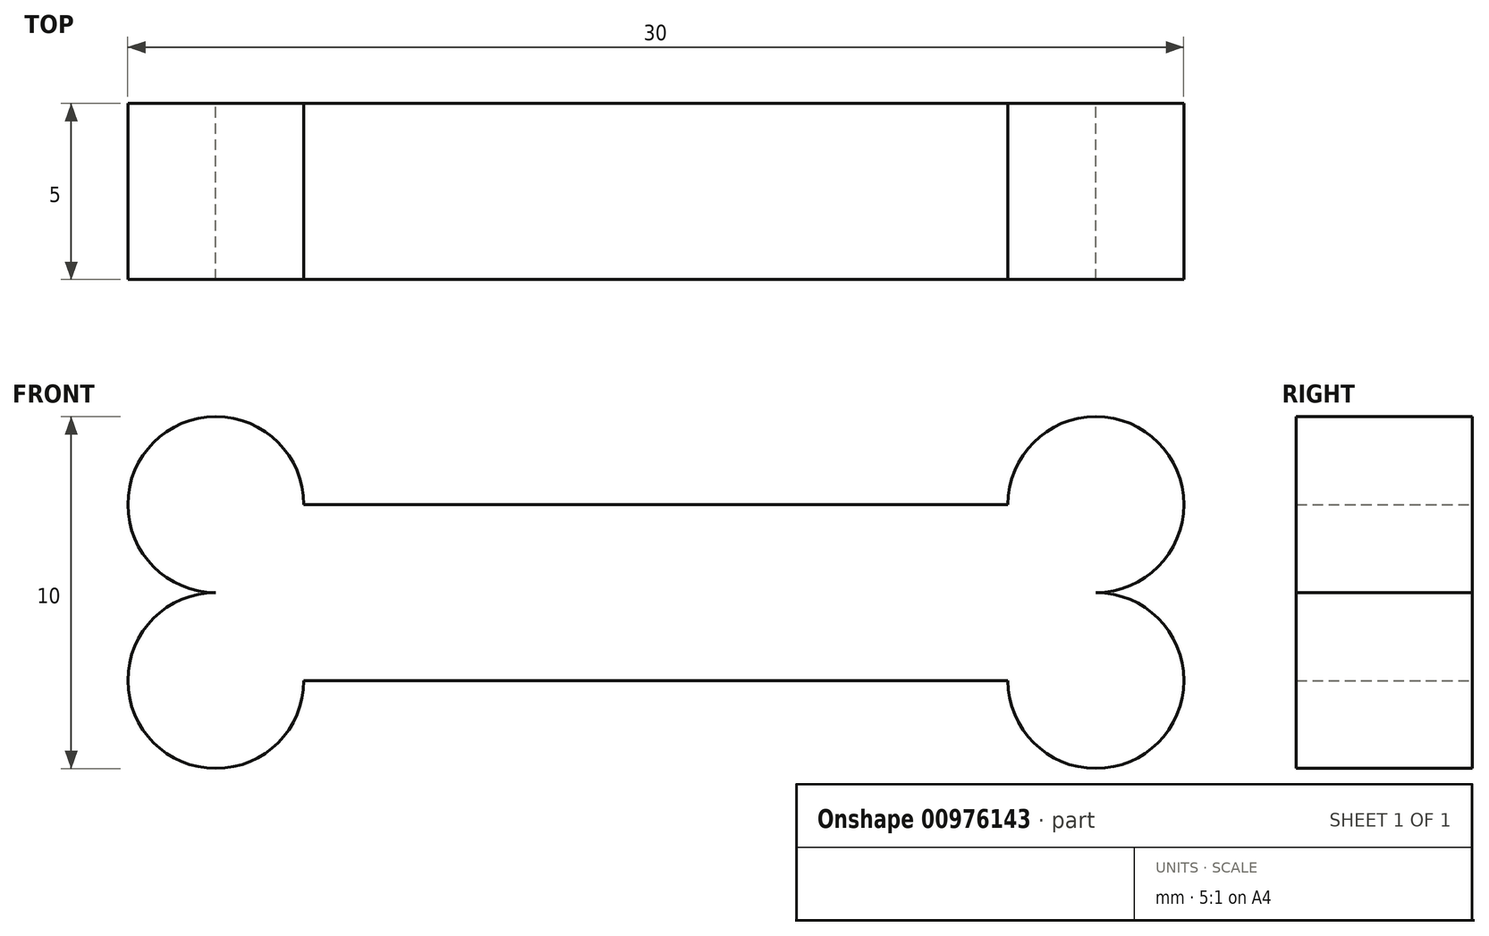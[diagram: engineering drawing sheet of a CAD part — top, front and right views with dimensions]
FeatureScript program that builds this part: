
annotation { "Feature Type Name" : "Feature", "Feature Type Description" : "" }
export const myFeature = defineFeature(function(context is Context, id is Id, definition is map)
    precondition{}
    {
        {
            var Q0;
            Q0=qCreatedBy(makeId("Front.planeOp"),FACE);
            var sketch = newSketch(context, id + "F0", { "sketchPlane" : qUnion([Q0])});
            skLineSegment(sketch, "E0.bottom", {"start": v(-36.88, -7.92) * mm, "end": v(-16.88, -7.92) * mm});
            skLineSegment(sketch, "E0.top", {"start": v(-36.88, -12.92) * mm, "end": v(-16.88, -12.92) * mm});
            skLineSegment(sketch, "E0.left", {"start": v(-39.38, -10.42) * mm, "end": v(-39.38, -10.42) * mm});
            skLineSegment(sketch, "E0.right", {"start": v(-14.38, -10.42) * mm, "end": v(-14.38, -10.42) * mm});
            skArc(sketch, "E1", {"start": v(-14.38, -10.42) * mm, "mid": v(-12.6, -6.15) * mm, "end": v(-16.88, -7.92) * mm});
            skArc(sketch, "E2", {"start": v(-16.88, -12.92) * mm, "mid": v(-12.6, -14.68) * mm, "end": v(-14.38, -10.42) * mm});
            skArc(sketch, "E3", {"start": v(-36.88, -7.92) * mm, "mid": v(-41.14, -6.15) * mm, "end": v(-39.38, -10.42) * mm});
            skArc(sketch, "E4", {"start": v(-39.38, -10.42) * mm, "mid": v(-41.14, -14.68) * mm, "end": v(-36.88, -12.92) * mm});
            skSolve(sketch);
        }
        {
            var Q0;
            Q0=makeQuery(id+"F0.imprint","IMPRINT",FACE,{"disambiguationData":[TD([[makeQuery(id+"F0.imprint","IMPRINT",EDGE,{"derivedFrom":sQuery(id+"F0.wireOp",EDGE,"E0.bottom")}),-1.0]])]});
            extrude(context, id + "F1", {"entities" : qUnion([Q0]), "depth" : 5 * mm, "offsetDistance" : 25 * mm});
        }
    });
